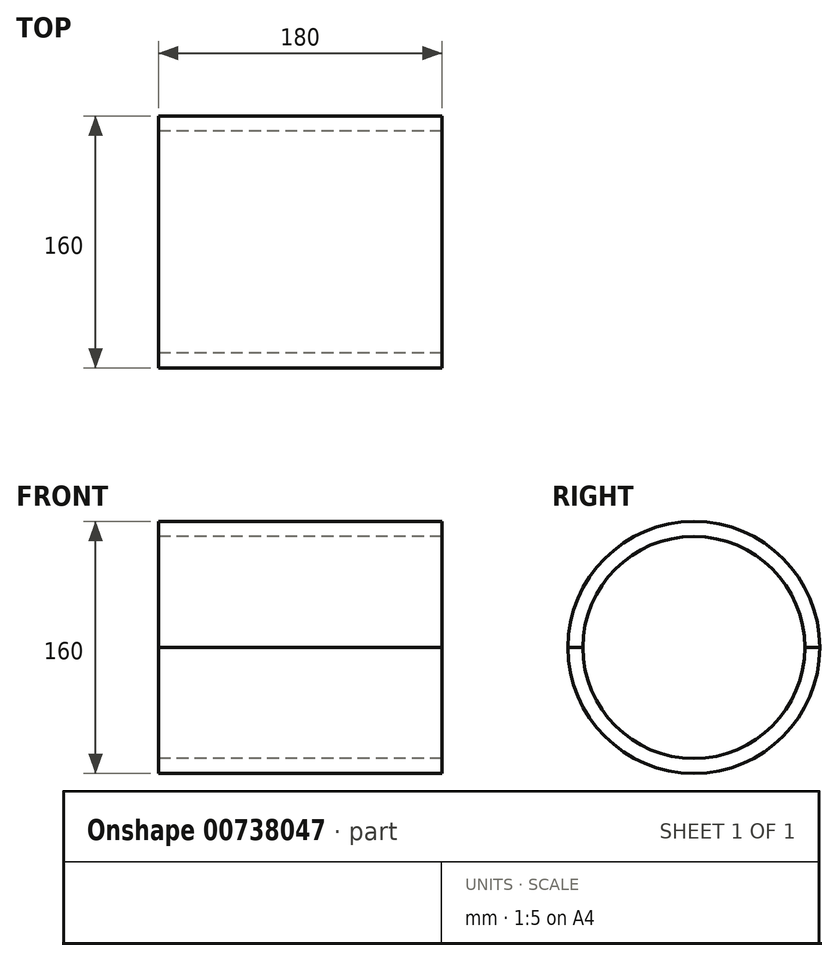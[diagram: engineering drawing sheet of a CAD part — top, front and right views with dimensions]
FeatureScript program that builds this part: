
annotation { "Feature Type Name" : "Feature", "Feature Type Description" : "" }
export const myFeature = defineFeature(function(context is Context, id is Id, definition is map)
    precondition{}
    {
        {
            var Q0;
            Q0=qCreatedBy(makeId("Front.planeOp"),FACE);
            var sketch = newSketch(context, id + "F0", { "sketchPlane" : qUnion([Q0])});
            skLineSegment(sketch, "E0.bottom", {"start": v(90, -80) * mm, "end": v(-90, -80) * mm});
            skLineSegment(sketch, "E0.top", {"start": v(90, 80) * mm, "end": v(-90, 80) * mm});
            skLineSegment(sketch, "E0.left", {"start": v(90, -80) * mm, "end": v(90, 80) * mm});
            skLineSegment(sketch, "E0.right", {"start": v(-90, -80) * mm, "end": v(-90, 80) * mm});
            skPoint(sketch, "E0.middle", {"position": v(0, 0) * mm});
            skLineSegment(sketch, "E1.bottom", {"start": v(90, -70.5) * mm, "end": v(-90, -70.5) * mm});
            skLineSegment(sketch, "E1.top", {"start": v(90, 70.5) * mm, "end": v(-90, 70.5) * mm});
            skLineSegment(sketch, "E1.left", {"start": v(90, -70.5) * mm, "end": v(90, 70.5) * mm});
            skLineSegment(sketch, "E1.right", {"start": v(-90, -70.5) * mm, "end": v(-90, 70.5) * mm});
            skLineSegment(sketch, "E2", {"start": v(0, 0) * mm, "end": v(200, 0) * mm, "construction": true});
            skSolve(sketch);
        }
        {
            var Q0;
            {var subQ0=sQuery(id+"F0.wireOp",EDGE,"E0.top");Q0=makeQuery(id+"F0.imprint","IMPRINT",FACE,{"disambiguationData":[TD([[makeQuery(id+"F0.imprint","IMPRINT",EDGE,{"derivedFrom":subQ0}),1.0]])]});}
            var Q1;
            {var subQ0=sQuery(id+"F0.wireOp",EDGE,"E0.bottom");Q1=makeQuery(id+"F0.imprint","IMPRINT",FACE,{"disambiguationData":[TD([[makeQuery(id+"F0.imprint","IMPRINT",EDGE,{"derivedFrom":subQ0}),-1.0]])]});}
            var Q2;
            Q2=sQuery(id+"F0.wireOp",EDGE,"E2");
            revolve(context, id + "F1", {"surfaceOperationType" : NewSurfaceOperationType.NEW, "entities" : qUnion([Q0, Q1]), "axis" : qUnion([Q2]), "revolveType" : RevolveType.SYMMETRIC, "angle" : 180 * degree});
        }
    });
